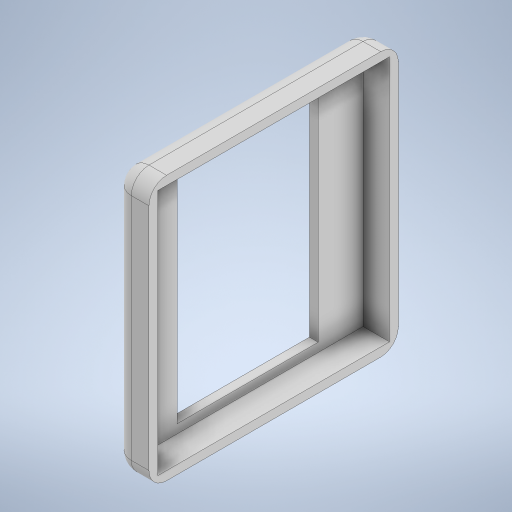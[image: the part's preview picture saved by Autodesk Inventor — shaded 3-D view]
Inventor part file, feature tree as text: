
AUTODESK INVENTOR PART (.ipt)
format: ipt  version: 2023 (Build 270158000, 158)  size: 270,336 bytes
history: native  units: in
note: dims shown in document units (in); Inventor stores cm internally (conversion verified against a paired STEP export)
features: extrude x2, fillet x2, sketch x2, shell x1
ambient origin geometry x8: Origin, YZ Plane, XZ Plane, XY Plane, X Axis, Y Axis, Z Axis, Center Point
bodies: Solid1 (feature_tree)
feature tree (7):
  extrude  "Extrusion1"  Depth=7.071in
  shell  "Shell1"  Thickness=1.0in
  extrude  "Extrusion2"  Depth=6.5in
  fillet  "Fillet1"  Radius=4.0in
  fillet  "Fillet2"  Radius=0.25in
  sketch  "Sketch1"  dims[d0=7.5in d1=7.071in d2=1.0in d3=0.0in]
  sketch  "Sketch2"  dims[d4=0.25in d5=6.5in d6=4.0in d7=0.25in d8=1.3in d9=0.0in d10=0.0in d11=0.5in d12=0.5in]
